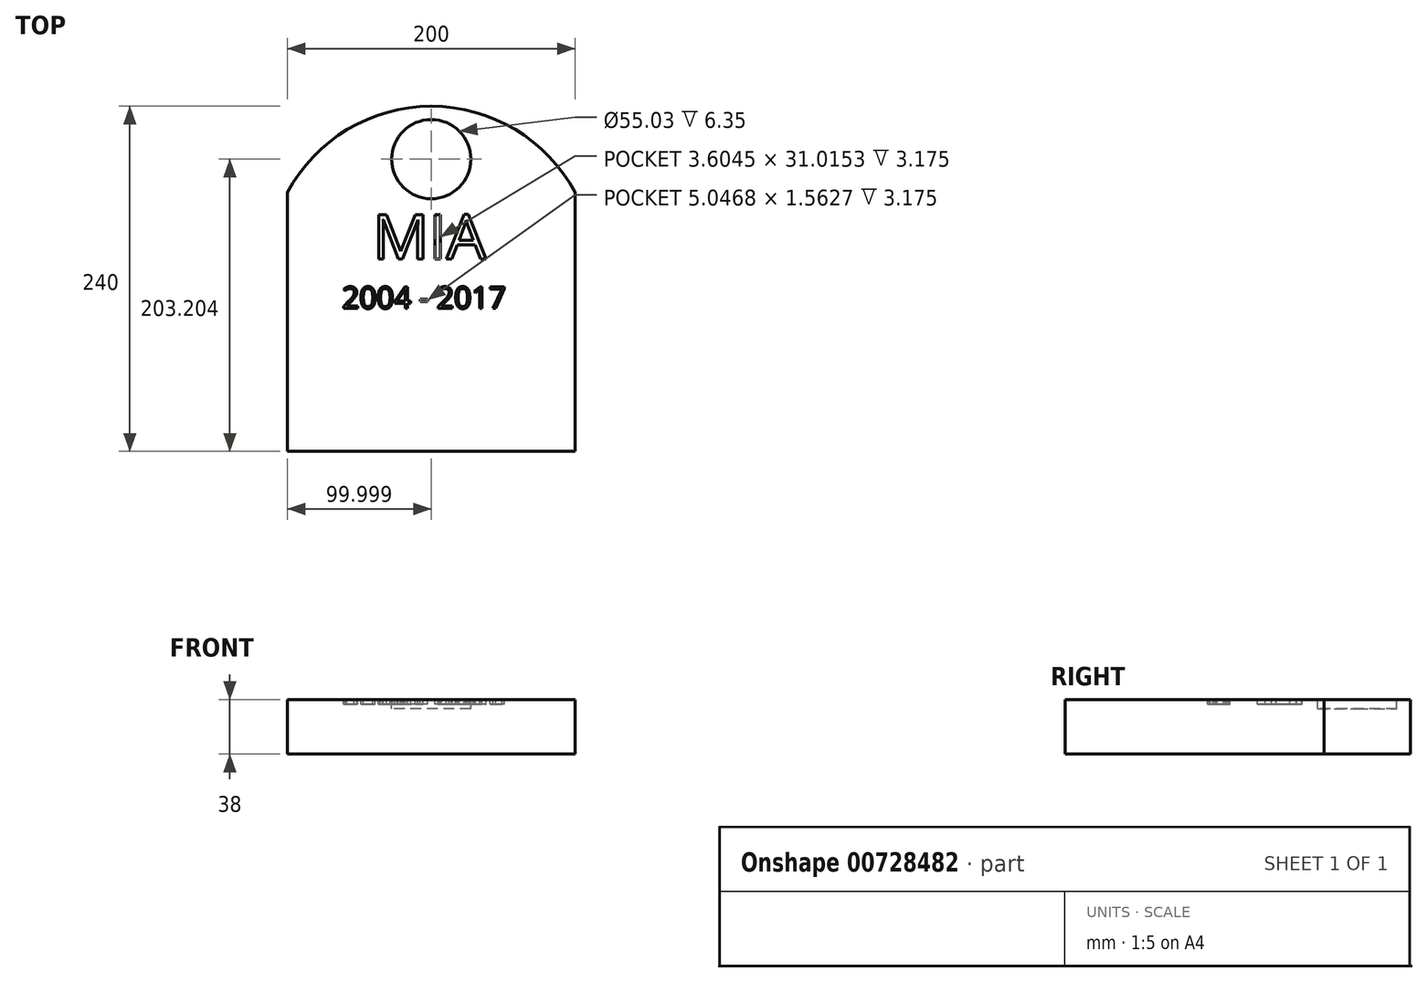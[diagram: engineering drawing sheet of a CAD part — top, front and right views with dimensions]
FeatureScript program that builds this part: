
annotation { "Feature Type Name" : "Feature", "Feature Type Description" : "" }
export const myFeature = defineFeature(function(context is Context, id is Id, definition is map)
    precondition{}
    {
        {
            var Q0;
            Q0=qCreatedBy(makeId("Top.planeOp"),FACE);
            var sketch = newSketch(context, id + "F0", { "sketchPlane" : qUnion([Q0])});
            skLineSegment(sketch, "E0.bottom", {"start": v(-83.4, 109.01) * mm, "end": v(116.6, 109.01) * mm});
            skLineSegment(sketch, "E0.top", {"start": v(-83.4, -70.99) * mm, "end": v(116.6, -70.99) * mm});
            skLineSegment(sketch, "E0.left", {"start": v(-83.4, 109.01) * mm, "end": v(-83.4, -70.99) * mm});
            skLineSegment(sketch, "E0.right", {"start": v(116.6, 109.01) * mm, "end": v(116.6, -70.99) * mm});
            skArc(sketch, "E1", {"start": v(116.6, 109.01) * mm, "mid": v(16.6, 169.01) * mm, "end": v(-83.4, 109.01) * mm});
            skPoint(sketch, "E2", {"position": v(16.6, 169.01) * mm});
            skSolve(sketch);
        }
        {
            var Q0;
            Q0=makeQuery(id+"F0.imprint","IMPRINT",FACE,{"disambiguationData":[TD([[makeQuery(id+"F0.imprint","IMPRINT",EDGE,{"derivedFrom":sQuery(id+"F0.wireOp",EDGE,"E0.bottom")}),1.0]])]});
            var Q1;
            Q1=makeQuery(id+"F0.imprint","IMPRINT",FACE,{"disambiguationData":[TD([[makeQuery(id+"F0.imprint","IMPRINT",EDGE,{"derivedFrom":sQuery(id+"F0.wireOp",EDGE,"E0.bottom")}),-1.0]])]});
            extrude(context, id + "F1", {"entities" : qUnion([Q0, Q1]), "depth" : 38 * mm, "offsetDistance" : 25 * mm});
        }
        {
            var Q0;
            Q0=makeQuery(id+"F1.opExtrude","CAP_FACE",FACE,{"disambiguationData":[OSD([sQuery(id+"F0.wireOp",EDGE,"E0.top"),sQuery(id+"F0.wireOp",EDGE,"E0.left"),sQuery(id+"F0.wireOp",EDGE,"E0.right"),sQuery(id+"F0.wireOp",EDGE,"E1")])],"isStart":false});
            var sketch = newSketch(context, id + "F2", { "sketchPlane" : qUnion([Q0])});
            skText(sketch, "E3", { "text": "MIA", "fontName": "OpenSans-Regular.ttf"});
            skPoint(sketch, "E4", {"position": v(16.6, 169.01) * mm});
            const initialGuessF2  = {"E3": [-0.02421, 0.06265, 1, 0, 0.03128]};
            skSetInitialGuess(sketch, initialGuessF2);
            skSolve(sketch);
        }
        {
            var Q0;
            Q0 = qSketchRegion(id + "F2", true);
            extrude(context, id + "F3", {"entities" : qUnion([Q0]), "operationType" : NewBodyOperationType.REMOVE, "oppositeDirection" : true, "depth" : 3.17 * mm, "offsetDistance" : 25 * mm});
        }
        {
            var Q0;
            {var subQ0=sQuery(id+"F0.wireOp",EDGE,"E0.left");var subQ1=sQuery(id+"F0.wireOp",EDGE,"E1");var subQ2=sQuery(id+"F0.wireOp",EDGE,"E0.top");var subQ3=sQuery(id+"F0.wireOp",EDGE,"E0.right");Q0=makeQuery(id+"F3.boolean.opBoolean","SPLIT",FACE,{"disambiguationData":[TD([makeQuery(id+"F1.opExtrude","SWEPT_FACE",FACE,{"disambiguationData":[OSD([subQ2])]})])],"derivedFrom":makeQuery(id+"F1.opExtrude","CAP_FACE",FACE,{"disambiguationData":[OSD([subQ2,subQ0,subQ3,subQ1])],"isStart":false})});}
            var sketch = newSketch(context, id + "F4", { "sketchPlane" : qUnion([Q0])});
            skCircle(sketch, "E5", {"center": v(16.6, 132.21) * mm, "radius": 27.51 * mm});
            skLineSegment(sketch, "E6", {"start": v(16.6, -70.99) * mm, "end": v(16.6, 335.41) * mm, "construction": true});
            skPoint(sketch, "E6.endSnap0", {"position": v(16.6, 169.01) * mm});
            skSolve(sketch);
        }
        {
            var Q0;
            Q0=makeQuery(id+"F4.imprint","IMPRINT",FACE,{"disambiguationData":[TD([[makeQuery(id+"F4.imprint","IMPRINT",EDGE,{"derivedFrom":sQuery(id+"F4.wireOp",EDGE,"E5")}),1.0]])]});
            extrude(context, id + "F5", {"entities" : qUnion([Q0]), "operationType" : NewBodyOperationType.REMOVE, "oppositeDirection" : true, "depth" : 6.35 * mm, "offsetDistance" : 25.4 * mm});
        }
        {
            var Q0;
            {var subQ0=sQuery(id+"F0.wireOp",EDGE,"E0.left");var subQ1=sQuery(id+"F0.wireOp",EDGE,"E1");var subQ2=sQuery(id+"F0.wireOp",EDGE,"E0.top");var subQ3=sQuery(id+"F0.wireOp",EDGE,"E0.right");Q0=makeQuery(id+"F3.boolean.opBoolean","SPLIT",FACE,{"disambiguationData":[TD([makeQuery(id+"F1.opExtrude","SWEPT_FACE",FACE,{"disambiguationData":[OSD([subQ2])]})])],"derivedFrom":makeQuery(id+"F1.opExtrude","CAP_FACE",FACE,{"disambiguationData":[OSD([subQ2,subQ0,subQ3,subQ1])],"isStart":false})});}
            var sketch = newSketch(context, id + "F6", { "sketchPlane" : qUnion([Q0])});
            skText(sketch, "E7", { "text": "2004 - 2017", "fontName": "OpenSans-Regular.ttf"});
            const initialGuessF6  = {"E7": [-0.0454, 0.02844, 1, 0, 0.01516]};
            skSetInitialGuess(sketch, initialGuessF6);
            skSolve(sketch);
        }
        {
            var Q0;
            Q0 = qSketchRegion(id + "F6", true);
            extrude(context, id + "F7", {"entities" : qUnion([Q0]), "operationType" : NewBodyOperationType.REMOVE, "oppositeDirection" : true, "depth" : 3.17 * mm, "offsetDistance" : 25.4 * mm});
        }
    });
